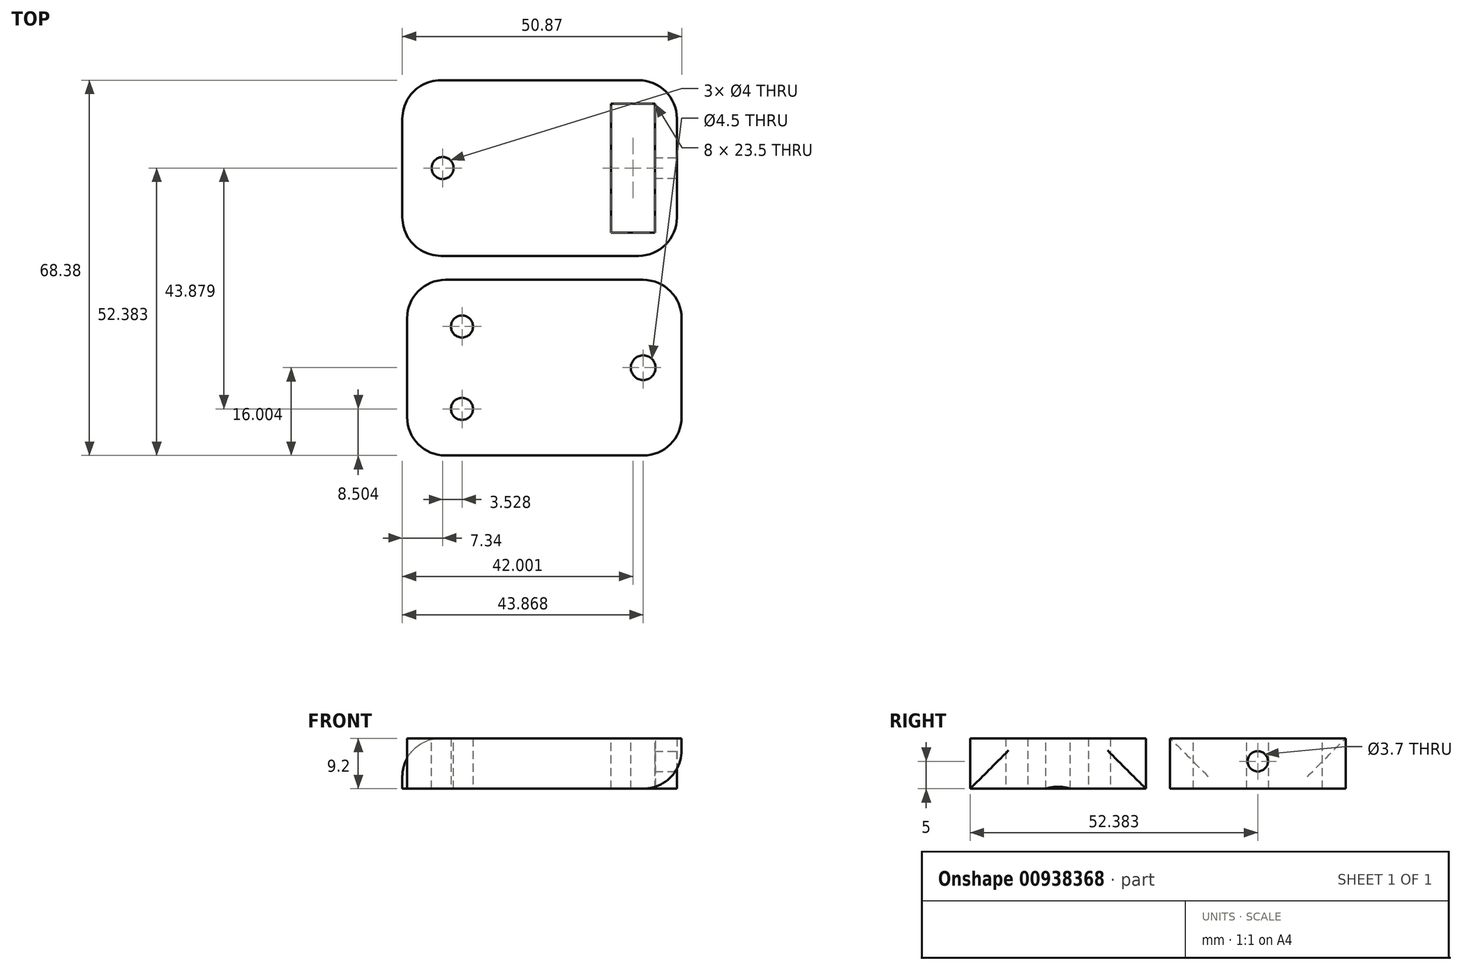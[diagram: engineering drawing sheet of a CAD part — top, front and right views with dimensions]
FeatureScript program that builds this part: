
annotation { "Feature Type Name" : "Feature", "Feature Type Description" : "" }
export const myFeature = defineFeature(function(context is Context, id is Id, definition is map)
    precondition{}
    {
        {
            var Q0;
            Q0=qCreatedBy(makeId("Top.planeOp"),FACE);
            var sketch = newSketch(context, id + "F0", { "sketchPlane" : qUnion([Q0])});
            skLineSegment(sketch, "E0.bottom", {"start": v(-31.96, 15.02) * mm, "end": v(18.04, 15.02) * mm});
            skLineSegment(sketch, "E0.top", {"start": v(-31.96, -16.98) * mm, "end": v(18.04, -16.98) * mm});
            skLineSegment(sketch, "E0.left", {"start": v(-31.96, 15.02) * mm, "end": v(-31.96, -16.98) * mm});
            skLineSegment(sketch, "E0.right", {"start": v(18.04, 15.02) * mm, "end": v(18.04, -16.98) * mm});
            skLineSegment(sketch, "E1.bottom", {"start": v(18.9, -53.36) * mm, "end": v(-31.1, -53.36) * mm});
            skLineSegment(sketch, "E1.top", {"start": v(18.9, -21.36) * mm, "end": v(-31.1, -21.36) * mm});
            skLineSegment(sketch, "E1.left", {"start": v(18.9, -53.36) * mm, "end": v(18.9, -21.36) * mm});
            skLineSegment(sketch, "E1.right", {"start": v(-31.1, -53.36) * mm, "end": v(-31.1, -21.36) * mm});
            skCircle(sketch, "E2", {"center": v(-21.1, -44.86) * mm, "radius": 2 * mm});
            skCircle(sketch, "E3", {"center": v(-21.1, -29.86) * mm, "radius": 2 * mm});
            skSolve(sketch);
        }
        {
            var Q0;
            Q0=qSketchRegion(id+"F0",true);
            extrude(context, id + "F1", {"entities" : qUnion([Q0]), "depth" : 9.2 * mm, "offsetDistance" : 25 * mm});
        }
        {
            var Q0;
            Q0=makeQuery(id+"F1.opExtrude","CAP_FACE",FACE,{"disambiguationData":[OSD([sQuery(id+"F0.wireOp",EDGE,"E0.bottom"),sQuery(id+"F0.wireOp",EDGE,"E0.top"),sQuery(id+"F0.wireOp",EDGE,"E0.left"),sQuery(id+"F0.wireOp",EDGE,"E0.right")])],"isStart":false});
            var sketch = newSketch(context, id + "F2", { "sketchPlane" : qUnion([Q0])});
            skLineSegment(sketch, "E4.bottom", {"start": v(6.04, 10.77) * mm, "end": v(14.04, 10.77) * mm});
            skLineSegment(sketch, "E4.top", {"start": v(6.04, -12.73) * mm, "end": v(14.04, -12.73) * mm});
            skLineSegment(sketch, "E4.left", {"start": v(6.04, 10.77) * mm, "end": v(6.04, -12.73) * mm});
            skLineSegment(sketch, "E4.right", {"start": v(14.04, 10.77) * mm, "end": v(14.04, -12.73) * mm});
            skCircle(sketch, "E5", {"center": v(-24.62, -0.98) * mm, "radius": 2 * mm});
            skSolve(sketch);
        }
        {
            var Q0;
            Q0=makeQuery(id+"F2.imprint","IMPRINT",FACE,{"disambiguationData":[TD([[makeQuery(id+"F2.imprint","IMPRINT",EDGE,{"derivedFrom":sQuery(id+"F2.wireOp",EDGE,"E4.bottom")}),-1.0]])]});
            var Q1;
            Q1=makeQuery(id+"F2.imprint","IMPRINT",FACE,{"disambiguationData":[TD([[makeQuery(id+"F2.imprint","IMPRINT",EDGE,{"derivedFrom":sQuery(id+"F2.wireOp",EDGE,"NCds5BFH-t4Id-2zwf-doRS-KX9CpPjDlQgJ")}),1.0]])]});
            var Q2;
            Q2=makeQuery(id+"F2.imprint","IMPRINT",FACE,{"disambiguationData":[TD([[makeQuery(id+"F2.imprint","IMPRINT",EDGE,{"derivedFrom":sQuery(id+"F2.wireOp",EDGE,"avfTDBd6-kbh5-bCmk-vPd7-ydhfcEMmiGgP")}),1.0]])]});
            var Q3;
            Q3=makeQuery(id+"F2.imprint","IMPRINT",FACE,{"disambiguationData":[TD([[makeQuery(id+"F2.imprint","IMPRINT",EDGE,{"derivedFrom":sQuery(id+"F2.wireOp",EDGE,"E5")}),1.0]])]});
            extrude(context, id + "F3", {"entities" : qUnion([Q0, Q1, Q2, Q3]), "operationType" : NewBodyOperationType.REMOVE, "oppositeDirection" : true, "depth" : 25 * mm, "offsetDistance" : 25 * mm});
        }
        {
            var Q0;
            Q0=makeQuery(id+"F1.opExtrude","SWEPT_FACE",FACE,{"disambiguationData":[OSD([sQuery(id+"F0.wireOp",EDGE,"E0.right")])]});
            var sketch = newSketch(context, id + "F4", { "sketchPlane" : qUnion([Q0])});
            skCircle(sketch, "E6", {"center": v(-0.98, 5) * mm, "radius": 1.85 * mm});
            skSolve(sketch);
        }
        {
            var Q0;
            Q0=qSketchRegion(id+"F4",true);
            var Q1;
            Q1=makeQuery(id+"F4.imprint","IMPRINT",FACE,{"disambiguationData":[TD([[makeQuery(id+"F4.imprint","IMPRINT",EDGE,{"derivedFrom":sQuery(id+"F4.wireOp",EDGE,"E6")}),1.0]])]});
            extrude(context, id + "F5", {"entities" : qUnion([Q0, Q1]), "operationType" : NewBodyOperationType.REMOVE, "oppositeDirection" : true, "depth" : 5 * mm, "offsetDistance" : 25 * mm});
        }
        {
            var Q0;
            Q0=makeQuery(id+"F1.opExtrude","CAP_FACE",FACE,{"disambiguationData":[OSD([sQuery(id+"F0.wireOp",EDGE,"E1.bottom"),sQuery(id+"F0.wireOp",EDGE,"E1.top"),sQuery(id+"F0.wireOp",EDGE,"E1.left"),sQuery(id+"F0.wireOp",EDGE,"E1.right"),sQuery(id+"F0.wireOp",EDGE,"E2"),sQuery(id+"F0.wireOp",EDGE,"E3")])],"isStart":false});
            var sketch = newSketch(context, id + "F6", { "sketchPlane" : qUnion([Q0])});
            skCircle(sketch, "E7", {"center": v(11.9, -37.36) * mm, "radius": 2.25 * mm});
            skSolve(sketch);
        }
        {
            var Q0;
            Q0=makeQuery(id+"F6.imprint","IMPRINT",FACE,{"disambiguationData":[TD([[makeQuery(id+"F6.imprint","IMPRINT",EDGE,{"derivedFrom":sQuery(id+"F6.wireOp",EDGE,"E7")}),1.0]])]});
            extrude(context, id + "F7", {"entities" : qUnion([Q0]), "operationType" : NewBodyOperationType.REMOVE, "oppositeDirection" : true, "depth" : 25 * mm, "offsetDistance" : 25 * mm});
        }
        {
            var Q0;
            Q0=makeQuery(id+"F1.opExtrude","SWEPT_EDGE",EDGE,{"disambiguationData":[OSD([sQuery(id+"F0.wireOp",EDGE,"E1.top"),sQuery(id+"F0.wireOp",EDGE,"E1.left")])]});
            var Q1;
            Q1=makeQuery(id+"F1.opExtrude","SWEPT_EDGE",EDGE,{"disambiguationData":[OSD([sQuery(id+"F0.wireOp",EDGE,"E1.bottom"),sQuery(id+"F0.wireOp",EDGE,"E1.left")])]});
            var Q2;
            Q2=makeQuery(id+"F1.opExtrude","CAP_EDGE",EDGE,{"disambiguationData":[OSD([sQuery(id+"F0.wireOp",EDGE,"E1.left")])],"isStart":true});
            var Q3;
            Q3=makeQuery(id+"F1.opExtrude","CAP_EDGE",EDGE,{"disambiguationData":[OSD([sQuery(id+"F0.wireOp",EDGE,"E0.left")])],"isStart":false});
            var Q4;
            Q4=makeQuery(id+"F1.opExtrude","SWEPT_EDGE",EDGE,{"disambiguationData":[OSD([sQuery(id+"F0.wireOp",EDGE,"E0.top"),sQuery(id+"F0.wireOp",EDGE,"E0.left")])]});
            var Q5;
            Q5=makeQuery(id+"F1.opExtrude","SWEPT_EDGE",EDGE,{"disambiguationData":[OSD([sQuery(id+"F0.wireOp",EDGE,"E0.bottom"),sQuery(id+"F0.wireOp",EDGE,"E0.left")])]});
            var Q6;
            Q6=makeQuery(id+"F1.opExtrude","SWEPT_EDGE",EDGE,{"disambiguationData":[OSD([sQuery(id+"F0.wireOp",EDGE,"E1.bottom"),sQuery(id+"F0.wireOp",EDGE,"E1.right")])]});
            var Q7;
            Q7=makeQuery(id+"F1.opExtrude","SWEPT_EDGE",EDGE,{"disambiguationData":[OSD([sQuery(id+"F0.wireOp",EDGE,"E1.top"),sQuery(id+"F0.wireOp",EDGE,"E1.right")])]});
            var Q8;
            Q8=makeQuery(id+"F1.opExtrude","SWEPT_EDGE",EDGE,{"disambiguationData":[OSD([sQuery(id+"F0.wireOp",EDGE,"E0.top"),sQuery(id+"F0.wireOp",EDGE,"E0.right")])]});
            var Q9;
            Q9=makeQuery(id+"F1.opExtrude","SWEPT_EDGE",EDGE,{"disambiguationData":[OSD([sQuery(id+"F0.wireOp",EDGE,"E0.bottom"),sQuery(id+"F0.wireOp",EDGE,"E0.right")])]});
            fillet(context, id + "F8", {"entities" : qUnion([Q0, Q1, Q2, Q3, Q4, Q5, Q6, Q7, Q8, Q9]), "tangentPropagation" : true, "radius" : 7 * mm, "defaultsChanged" : false, "vertexSettings" : [], "allowEdgeOverflow" : false});
        }
    });
